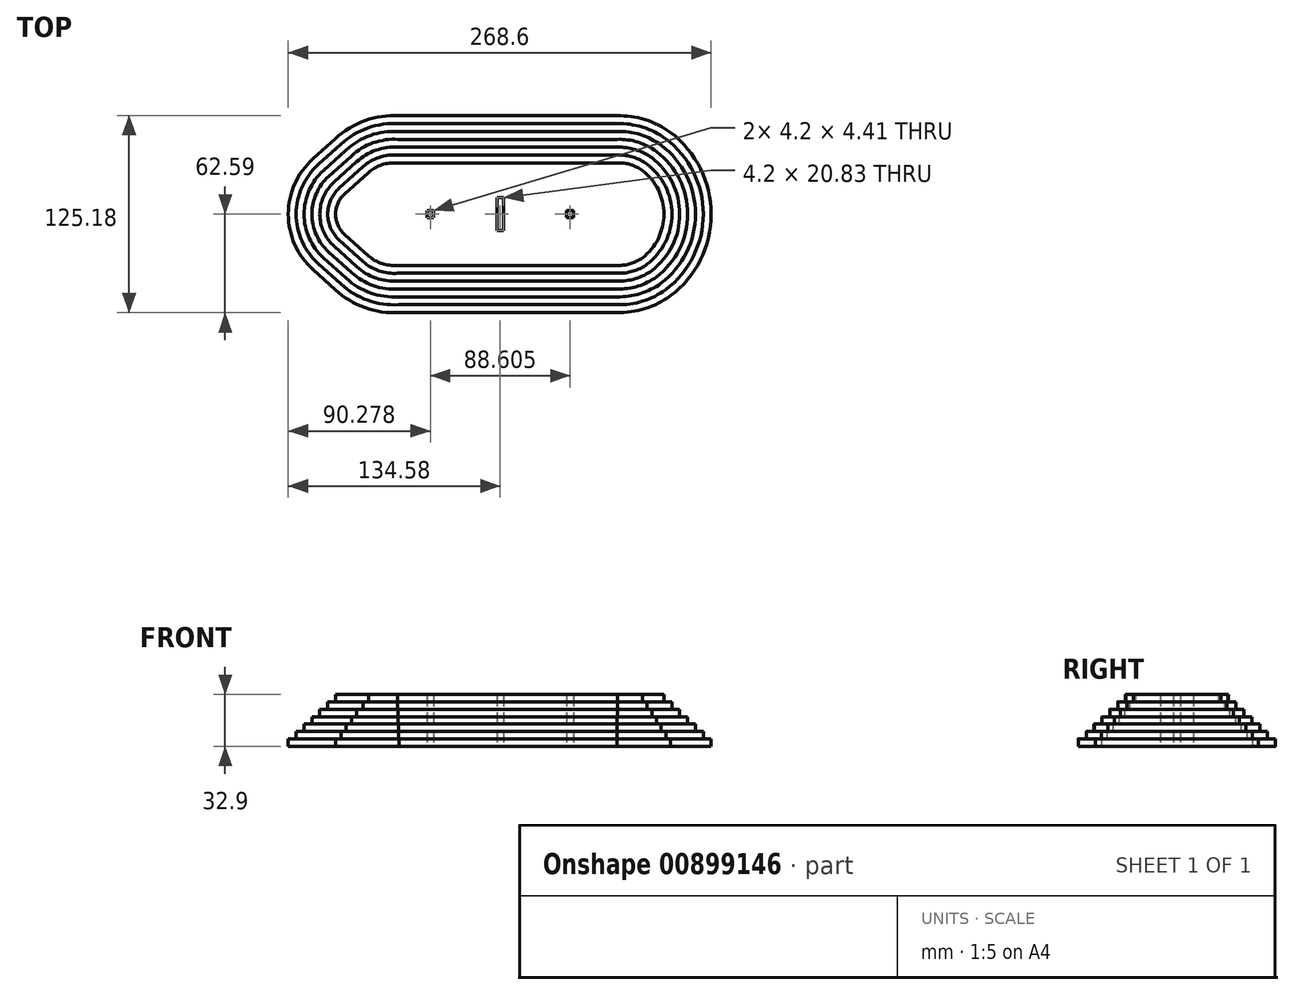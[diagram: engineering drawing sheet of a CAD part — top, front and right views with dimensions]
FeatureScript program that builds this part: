
annotation { "Feature Type Name" : "Feature", "Feature Type Description" : "" }
export const myFeature = defineFeature(function(context is Context, id is Id, definition is map)
    precondition{}
    {
        {
            var Q0;
            Q0=qCreatedBy(makeId("Top.planeOp"),FACE);
            var sketch = newSketch(context, id + "F0", { "sketchPlane" : qUnion([Q0])});
            skLineSegment(sketch, "E0.left", {"start": v(-75, 16.79) * mm, "end": v(-75, -16.79) * mm});
            skLineSegment(sketch, "E0.right", {"start": v(75, 17.5) * mm, "end": v(75, 0) * mm});
            skPoint(sketch, "E0.middle", {"position": v(0, 0) * mm});
            skPoint(sketch, "E1.endSnap0", {"position": v(-75, 0) * mm});
            skPoint(sketch, "E2", {"position": v(-3.7, 0) * mm});
            skLineSegment(sketch, "E3", {"start": v(-3.7, 0) * mm, "end": v(-92.3, 0) * mm});
            skLineSegment(sketch, "E4", {"start": v(-3.7, 0) * mm, "end": v(85.32, 0) * mm});
            skLineSegment(sketch, "E5", {"start": v(-92.51, 1.72) * mm, "end": v(-92.51, -1.72) * mm});
            skPoint(sketch, "E6.orphan", {"position": v(-94.42, 0) * mm});
            skPoint(sketch, "E7", {"position": v(-48, 0) * mm});
            skPoint(sketch, "E8", {"position": v(40.8, 0) * mm});
            skLineSegment(sketch, "E9.bottom", {"start": v(-50.1, 2.2) * mm, "end": v(-45.9, 2.2) * mm});
            skLineSegment(sketch, "E9.top", {"start": v(-50.1, -2.2) * mm, "end": v(-45.9, -2.2) * mm});
            skLineSegment(sketch, "E9.left", {"start": v(-50.1, 2.2) * mm, "end": v(-50.1, -2.2) * mm});
            skLineSegment(sketch, "E9.right", {"start": v(-45.9, 2.2) * mm, "end": v(-45.9, -2.2) * mm});
            skLineSegment(sketch, "E10", {"start": v(-3.7, 0) * mm, "end": v(-3.7, 17.5) * mm});
            skLineSegment(sketch, "E11.MirrorCS", {"start": v(38.5, 2.2) * mm, "end": v(38.5, -2.2) * mm});
            skLineSegment(sketch, "E12.MirrorCS", {"start": v(42.7, 2.2) * mm, "end": v(38.5, 2.2) * mm});
            skLineSegment(sketch, "E13.MirrorCS", {"start": v(42.7, 2.2) * mm, "end": v(42.7, -2.2) * mm});
            skLineSegment(sketch, "E14.MirrorCS", {"start": v(42.7, -2.2) * mm, "end": v(38.5, -2.2) * mm});
            skLineSegment(sketch, "E15.bottom", {"start": v(-5.8, 10.42) * mm, "end": v(-1.6, 10.42) * mm});
            skLineSegment(sketch, "E15.top", {"start": v(-5.8, -10.42) * mm, "end": v(-1.6, -10.42) * mm});
            skLineSegment(sketch, "E15.left", {"start": v(-5.8, 10.42) * mm, "end": v(-5.8, -10.42) * mm});
            skLineSegment(sketch, "E15.right", {"start": v(-1.6, 10.42) * mm, "end": v(-1.6, -10.42) * mm});
            skPoint(sketch, "E16.orphan", {"position": v(-75, 17.5) * mm});
            skPoint(sketch, "E17.orphan", {"position": v(-75, -17.5) * mm});
            skArc(sketch, "E18", {"start": v(-92.51, 1.72) * mm, "mid": v(-93.28, 0) * mm, "end": v(-92.51, -1.72) * mm});
            skArc(sketch, "E19.4", {"start": v(80.71, 19.7) * mm, "mid": v(80.68, 19.72) * mm, "end": v(80.64, 19.75) * mm});
            skArc(sketch, "E20.0", {"start": v(-68.99, 32.5) * mm, "mid": v(-78.84, 31.36) * mm, "end": v(-87.47, 26.46) * mm});
            skLineSegment(sketch, "E20.1", {"start": v(-87.47, 26.46) * mm, "end": v(-102.55, 12.87) * mm});
            skLineSegment(sketch, "E20.2", {"start": v(-68.99, 32.5) * mm, "end": v(70.9, 32.5) * mm});
            skArc(sketch, "E20.3", {"start": v(-102.55, 12.87) * mm, "mid": v(-108.28, 0) * mm, "end": v(-102.55, -12.87) * mm});
            skLineSegment(sketch, "E20.4", {"start": v(-102.55, -12.87) * mm, "end": v(-87.47, -26.46) * mm});
            skArc(sketch, "E20.5", {"start": v(-68.99, -32.5) * mm, "mid": v(-78.84, -31.36) * mm, "end": v(-87.47, -26.46) * mm});
            skArc(sketch, "E20.6", {"start": v(86.61, 27.78) * mm, "mid": v(79.15, 31.46) * mm, "end": v(70.9, 32.5) * mm});
            skArc(sketch, "E20.7", {"start": v(86.61, -27.78) * mm, "mid": v(100.32, 0) * mm, "end": v(86.61, 27.78) * mm});
            skArc(sketch, "E20.8", {"start": v(86.61, -27.78) * mm, "mid": v(79.15, -31.46) * mm, "end": v(70.9, -32.5) * mm});
            skLineSegment(sketch, "E20.9", {"start": v(-68.99, -32.5) * mm, "end": v(70.9, -32.5) * mm});
            skArc(sketch, "E21.0", {"start": v(-68.79, 37.5) * mm, "mid": v(-80.52, 36.07) * mm, "end": v(-90.79, 30.2) * mm});
            skLineSegment(sketch, "E21.1", {"start": v(-90.79, 30.2) * mm, "end": v(-105.9, 16.58) * mm});
            skLineSegment(sketch, "E21.2", {"start": v(-68.79, 37.5) * mm, "end": v(70.8, 37.5) * mm});
            skArc(sketch, "E21.3", {"start": v(-105.9, 16.58) * mm, "mid": v(-113.28, 0) * mm, "end": v(-105.9, -16.58) * mm});
            skLineSegment(sketch, "E21.4", {"start": v(-105.9, -16.58) * mm, "end": v(-90.79, -30.2) * mm});
            skArc(sketch, "E21.5", {"start": v(-68.79, -37.5) * mm, "mid": v(-80.52, -36.07) * mm, "end": v(-90.79, -30.2) * mm});
            skArc(sketch, "E21.6", {"start": v(89.6, 31.79) * mm, "mid": v(80.68, 36.22) * mm, "end": v(70.8, 37.5) * mm});
            skArc(sketch, "E21.7", {"start": v(89.6, -31.79) * mm, "mid": v(105.32, 0) * mm, "end": v(89.6, 31.79) * mm});
            skArc(sketch, "E21.8", {"start": v(89.6, -31.79) * mm, "mid": v(80.68, -36.22) * mm, "end": v(70.8, -37.5) * mm});
            skLineSegment(sketch, "E21.9", {"start": v(-68.79, -37.5) * mm, "end": v(70.8, -37.5) * mm});
            skArc(sketch, "E22.0", {"start": v(-68.6, 42.5) * mm, "mid": v(-82.67, 40.62) * mm, "end": v(-94.83, 33.29) * mm});
            skLineSegment(sketch, "E22.1", {"start": v(-94.83, 33.29) * mm, "end": v(-109.25, 20.3) * mm});
            skLineSegment(sketch, "E22.2", {"start": v(-68.6, 42.5) * mm, "end": v(70.7, 42.5) * mm});
            skArc(sketch, "E22.3", {"start": v(-109.25, 20.3) * mm, "mid": v(-118.28, 0) * mm, "end": v(-109.25, -20.3) * mm});
            skLineSegment(sketch, "E22.4", {"start": v(-109.25, -20.3) * mm, "end": v(-94.83, -33.29) * mm});
            skArc(sketch, "E22.5", {"start": v(-68.6, -42.5) * mm, "mid": v(-82.67, -40.62) * mm, "end": v(-94.83, -33.29) * mm});
            skArc(sketch, "E22.6", {"start": v(92.58, 35.8) * mm, "mid": v(82.2, 40.98) * mm, "end": v(70.7, 42.5) * mm});
            skArc(sketch, "E22.7", {"start": v(92.58, -35.8) * mm, "mid": v(110.32, 0) * mm, "end": v(92.58, 35.8) * mm});
            skArc(sketch, "E22.8", {"start": v(92.58, -35.8) * mm, "mid": v(82.2, -40.98) * mm, "end": v(70.7, -42.5) * mm});
            skLineSegment(sketch, "E22.9", {"start": v(-68.6, -42.5) * mm, "end": v(70.7, -42.5) * mm});
            skLineSegment(sketch, "E23.0", {"start": v(-68.79, 37.5) * mm, "end": v(70.7, 37.5) * mm});
            skArc(sketch, "E23.1", {"start": v(-68.79, 37.5) * mm, "mid": v(-80.95, 35.92) * mm, "end": v(-91.45, 29.6) * mm});
            skLineSegment(sketch, "E23.2", {"start": v(-91.45, 29.6) * mm, "end": v(-105.9, 16.58) * mm});
            skArc(sketch, "E24.0", {"start": v(-68.43, 47.5) * mm, "mid": v(-84.4, 45.3) * mm, "end": v(-98.2, 36.98) * mm});
            skLineSegment(sketch, "E24.1", {"start": v(-98.2, 36.98) * mm, "end": v(-112.6, 24.01) * mm});
            skLineSegment(sketch, "E24.2", {"start": v(-68.43, 47.5) * mm, "end": v(70.62, 47.5) * mm});
            skArc(sketch, "E24.3", {"start": v(-112.6, 24.01) * mm, "mid": v(-123.28, 0) * mm, "end": v(-112.6, -24.01) * mm});
            skLineSegment(sketch, "E24.4", {"start": v(-112.6, -24.01) * mm, "end": v(-98.2, -36.98) * mm});
            skArc(sketch, "E24.5", {"start": v(-68.43, -47.5) * mm, "mid": v(-84.4, -45.3) * mm, "end": v(-98.2, -36.98) * mm});
            skArc(sketch, "E24.6", {"start": v(95.57, 39.8) * mm, "mid": v(83.74, 45.74) * mm, "end": v(70.62, 47.5) * mm});
            skArc(sketch, "E24.7", {"start": v(95.57, -39.8) * mm, "mid": v(115.32, 0) * mm, "end": v(95.57, 39.8) * mm});
            skArc(sketch, "E24.8", {"start": v(95.57, -39.8) * mm, "mid": v(83.74, -45.74) * mm, "end": v(70.62, -47.5) * mm});
            skLineSegment(sketch, "E24.9", {"start": v(-68.43, -47.5) * mm, "end": v(70.62, -47.5) * mm});
            skLineSegment(sketch, "E25.0", {"start": v(-68.43, 42.5) * mm, "end": v(70.62, 42.5) * mm});
            skArc(sketch, "E26.0", {"start": v(-68.27, 52.5) * mm, "mid": v(-86.13, 50) * mm, "end": v(-101.57, 40.67) * mm});
            skLineSegment(sketch, "E26.1", {"start": v(-101.57, 40.67) * mm, "end": v(-115.94, 27.72) * mm});
            skLineSegment(sketch, "E26.2", {"start": v(-68.27, 52.5) * mm, "end": v(70.54, 52.5) * mm});
            skArc(sketch, "E26.3", {"start": v(-115.94, 27.72) * mm, "mid": v(-128.28, 0) * mm, "end": v(-115.94, -27.72) * mm});
            skLineSegment(sketch, "E26.4", {"start": v(-115.94, -27.72) * mm, "end": v(-101.57, -40.67) * mm});
            skArc(sketch, "E26.5", {"start": v(-68.27, -52.5) * mm, "mid": v(-86.13, -50) * mm, "end": v(-101.57, -40.67) * mm});
            skArc(sketch, "E26.6", {"start": v(98.56, 43.82) * mm, "mid": v(85.27, 50.5) * mm, "end": v(70.54, 52.5) * mm});
            skArc(sketch, "E26.7", {"start": v(98.56, -43.82) * mm, "mid": v(120.32, 0) * mm, "end": v(98.56, 43.82) * mm});
            skArc(sketch, "E26.8", {"start": v(98.56, -43.82) * mm, "mid": v(85.27, -50.5) * mm, "end": v(70.54, -52.5) * mm});
            skLineSegment(sketch, "E26.9", {"start": v(-68.27, -52.5) * mm, "end": v(70.54, -52.5) * mm});
            skLineSegment(sketch, "E27.0", {"start": v(-68.11, 57.5) * mm, "end": v(70.46, 57.5) * mm});
            skArc(sketch, "E27.1", {"start": v(101.55, 47.83) * mm, "mid": v(86.81, 55.26) * mm, "end": v(70.46, 57.5) * mm});
            skArc(sketch, "E27.2", {"start": v(-68.11, 57.5) * mm, "mid": v(-87.86, 54.7) * mm, "end": v(-104.94, 44.37) * mm});
            skArc(sketch, "E27.3", {"start": v(101.55, -47.83) * mm, "mid": v(125.32, 0) * mm, "end": v(101.55, 47.83) * mm});
            skArc(sketch, "E27.4", {"start": v(101.55, -47.83) * mm, "mid": v(86.81, -55.26) * mm, "end": v(70.46, -57.5) * mm});
            skLineSegment(sketch, "E27.5", {"start": v(-68.11, -57.5) * mm, "end": v(70.46, -57.5) * mm});
            skLineSegment(sketch, "E27.6", {"start": v(-104.94, 44.37) * mm, "end": v(-119.29, 31.44) * mm});
            skArc(sketch, "E27.7", {"start": v(-119.29, 31.44) * mm, "mid": v(-133.28, 0) * mm, "end": v(-119.29, -31.44) * mm});
            skLineSegment(sketch, "E27.8", {"start": v(-119.29, -31.44) * mm, "end": v(-104.94, -44.37) * mm});
            skArc(sketch, "E27.9", {"start": v(-68.11, -57.5) * mm, "mid": v(-87.86, -54.7) * mm, "end": v(-104.94, -44.37) * mm});
            skArc(sketch, "E28.0", {"start": v(-67.97, 62.5) * mm, "mid": v(-89.6, 59.38) * mm, "end": v(-108.3, 48.07) * mm});
            skLineSegment(sketch, "E28.1", {"start": v(-108.3, 48.07) * mm, "end": v(-122.63, 35.15) * mm});
            skLineSegment(sketch, "E28.2", {"start": v(-67.97, 62.5) * mm, "end": v(70.4, 62.5) * mm});
            skArc(sketch, "E28.3", {"start": v(-122.63, 35.15) * mm, "mid": v(-138.28, 0) * mm, "end": v(-122.63, -35.15) * mm});
            skLineSegment(sketch, "E28.4", {"start": v(-122.63, -35.15) * mm, "end": v(-108.3, -48.07) * mm});
            skArc(sketch, "E28.5", {"start": v(-67.97, -62.5) * mm, "mid": v(-89.6, -59.38) * mm, "end": v(-108.3, -48.07) * mm});
            skArc(sketch, "E28.6", {"start": v(104.54, 51.84) * mm, "mid": v(88.35, 60.02) * mm, "end": v(70.4, 62.5) * mm});
            skArc(sketch, "E28.7", {"start": v(104.54, -51.84) * mm, "mid": v(130.32, 0) * mm, "end": v(104.54, 51.84) * mm});
            skArc(sketch, "E28.8", {"start": v(104.54, -51.84) * mm, "mid": v(88.35, -60.02) * mm, "end": v(70.4, -62.5) * mm});
            skLineSegment(sketch, "E28.9", {"start": v(-67.97, -62.5) * mm, "end": v(70.4, -62.5) * mm});
            skLineSegment(sketch, "E29.trimOffspring", {"start": v(75, -17.04) * mm, "end": v(75, -17.5) * mm});
            skPoint(sketch, "E30.MirrorCS.end.orphan", {"position": v(71.28, -17.5) * mm});
            skPoint(sketch, "E31.orphan", {"position": v(77.67, -15.73) * mm});
            skPoint(sketch, "E32.orphan", {"position": v(77.67, 15.73) * mm});
            skPoint(sketch, "E33.end.orphan", {"position": v(71.28, 17.5) * mm});
            skSolve(sketch);
        }
        {
            var Q0;
            Q0=makeQuery(id+"F0.imprint","IMPRINT",FACE,{"disambiguationData":[TD([[makeQuery(id+"F0.imprint","IMPRINT",EDGE,{"derivedFrom":sQuery(id+"F0.wireOp",EDGE,"E27.0")}),1.0]])]});
            extrude(context, id + "F1", {"entities" : qUnion([Q0]), "depth" : 4.7 * mm, "offsetDistance" : 25 * mm});
        }
        {
            var Q0;
            Q0=makeQuery(id+"F0.imprint","IMPRINT",FACE,{"disambiguationData":[TD([[makeQuery(id+"F0.imprint","IMPRINT",EDGE,{"derivedFrom":sQuery(id+"F0.wireOp",EDGE,"E26.0")}),-1.0]])]});
            extrude(context, id + "F2", {"entities" : qUnion([Q0]), "operationType" : NewBodyOperationType.ADD, "depth" : (4.7 + 4.7) * mm, "offsetDistance" : 25 * mm});
        }
        {
            var Q0;
            Q0=makeQuery(id+"F0.imprint","IMPRINT",FACE,{"disambiguationData":[TD([[makeQuery(id+"F0.imprint","IMPRINT",EDGE,{"derivedFrom":sQuery(id+"F0.wireOp",EDGE,"E24.0")}),-1.0]])]});
            extrude(context, id + "F3", {"entities" : qUnion([Q0]), "operationType" : NewBodyOperationType.ADD, "depth" : (4.7 + 4.7 + 4.7) * mm, "offsetDistance" : 25 * mm});
        }
        {
            var Q0;
            {var subQ3=sQuery(id+"F0.wireOp",EDGE,"E22.0");Q0=makeQuery(id+"F0.imprint","IMPRINT",FACE,{"disambiguationData":[TD([[makeQuery(id+"F0.imprint","IMPRINT",EDGE,{"derivedFrom":subQ3}),-1.0]])]});}
            extrude(context, id + "F4", {"entities" : qUnion([Q0]), "operationType" : NewBodyOperationType.ADD, "depth" : (4.7 + 4.7 + 4.7 + 4.7) * mm, "offsetDistance" : 25 * mm});
        }
        {
            var Q0;
            {var subQ8=sQuery(id+"F0.wireOp",EDGE,"E21.0");Q0=makeQuery(id+"F0.imprint","IMPRINT",FACE,{"disambiguationData":[TD([[makeQuery(id+"F0.imprint","IMPRINT",EDGE,{"derivedFrom":subQ8}),-1.0]])]});}
            extrude(context, id + "F5", {"entities" : qUnion([Q0]), "operationType" : NewBodyOperationType.ADD, "depth" : (4.7 + 4.7 + 4.7 + 4.7 + 4.7) * mm, "offsetDistance" : 25 * mm});
        }
        {
            var Q0;
            Q0=makeQuery(id+"F0.imprint","IMPRINT",FACE,{"disambiguationData":[TD([[makeQuery(id+"F0.imprint","IMPRINT",EDGE,{"derivedFrom":sQuery(id+"F0.wireOp",EDGE,"E20.0")}),-1.0]])]});
            extrude(context, id + "F6", {"entities" : qUnion([Q0]), "operationType" : NewBodyOperationType.ADD, "depth" : (4.7 + 4.7 + 4.7 + 4.7 + 4.7 + 4.7) * mm, "offsetDistance" : 25 * mm});
        }
        {
            var Q0;
            Q0=makeQuery(id+"F0.imprint","IMPRINT",FACE,{"disambiguationData":[TD([[makeQuery(id+"F0.imprint","IMPRINT",EDGE,{"derivedFrom":sQuery(id+"F0.wireOp",EDGE,"E5")}),1.0]])]});
            var Q1;
            Q1=makeQuery(id+"F0.imprint","IMPRINT",FACE,{"disambiguationData":[TD([[makeQuery(id+"F0.imprint","IMPRINT",EDGE,{"derivedFrom":sQuery(id+"F0.wireOp",EDGE,"E5")}),-1.0]])]});
            extrude(context, id + "F7", {"entities" : qUnion([Q0, Q1]), "operationType" : NewBodyOperationType.ADD, "depth" : (4.7 * 7) * mm, "offsetDistance" : 25 * mm});
        }
    });
